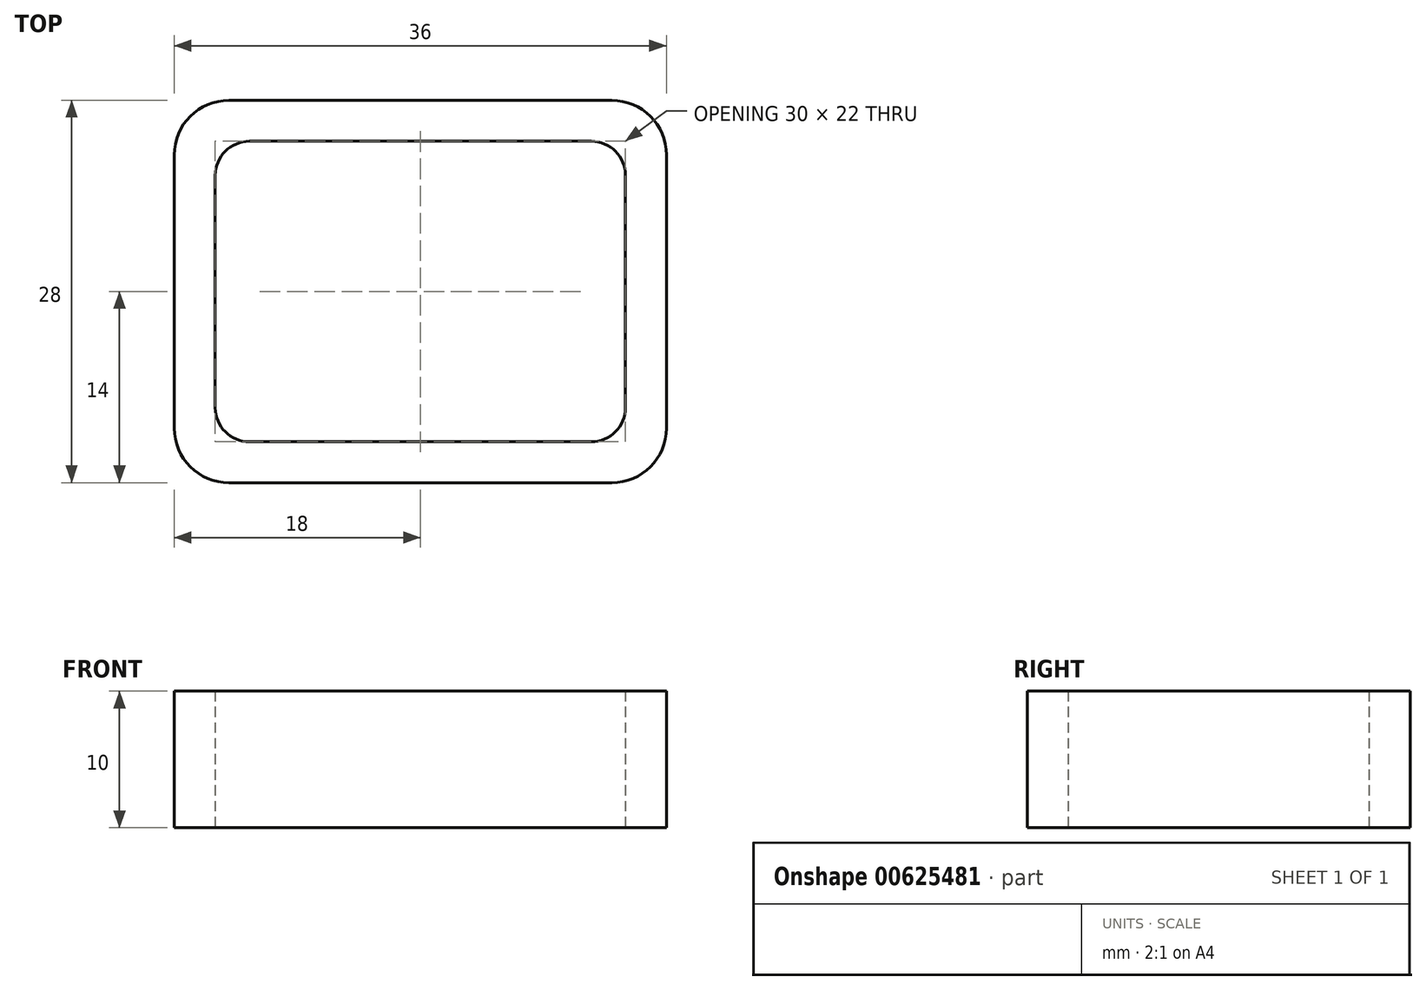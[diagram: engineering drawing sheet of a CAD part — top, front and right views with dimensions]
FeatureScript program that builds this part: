
annotation { "Feature Type Name" : "Feature", "Feature Type Description" : "" }
export const myFeature = defineFeature(function(context is Context, id is Id, definition is map)
    precondition{}
    {
        {
            var Q0;
            Q0=qCreatedBy(makeId("Top.planeOp"),FACE);
            var sketch = newSketch(context, id + "F0", { "sketchPlane" : qUnion([Q0])});
            skLineSegment(sketch, "E0.bottom", {"start": v(18, -14) * mm, "end": v(-18, -14) * mm});
            skLineSegment(sketch, "E0.top", {"start": v(18, 14) * mm, "end": v(-18, 14) * mm});
            skLineSegment(sketch, "E0.left", {"start": v(18, -14) * mm, "end": v(18, 14) * mm});
            skLineSegment(sketch, "E0.right", {"start": v(-18, -14) * mm, "end": v(-18, 14) * mm});
            skPoint(sketch, "E0.middle", {"position": v(0, 0) * mm});
            skSolve(sketch);
        }
        {
            var Q0;
            Q0 = qSketchRegion(id + "F0", true);
            extrude(context, id + "F1", {"entities" : qUnion([Q0]), "depth" : 10 * mm, "offsetDistance" : 25 * mm});
        }
        {
            var Q0;
            Q0=makeQuery(id+"F1.opExtrude","CAP_FACE",FACE,{"disambiguationData":[OSD([sQuery(id+"F0.wireOp",EDGE,"E0.bottom"),sQuery(id+"F0.wireOp",EDGE,"E0.top"),sQuery(id+"F0.wireOp",EDGE,"E0.left"),sQuery(id+"F0.wireOp",EDGE,"E0.right")])],"isStart":false});
            var Q1;
            Q1=makeQuery(id+"F1.opExtrude","CAP_FACE",FACE,{"disambiguationData":[OSD([sQuery(id+"F0.wireOp",EDGE,"E0.bottom"),sQuery(id+"F0.wireOp",EDGE,"E0.top"),sQuery(id+"F0.wireOp",EDGE,"E0.left"),sQuery(id+"F0.wireOp",EDGE,"E0.right")])],"isStart":true});
            shell(context, id + "F2", {"entities" : qUnion([Q0, Q1]), "thickness" : 3 * mm});
        }
        {
            var Q0;
            Q0=makeQuery(id+"F2.opShell","OFFSET_EDGE",EDGE,{"disambiguationData":[OSD([sQuery(id+"F0.wireOp",EDGE,"E0.top"),sQuery(id+"F0.wireOp",EDGE,"E0.right")])]});
            var Q1;
            Q1=makeQuery(id+"F2.opShell","OFFSET_EDGE",EDGE,{"disambiguationData":[OSD([sQuery(id+"F0.wireOp",EDGE,"E0.top"),sQuery(id+"F0.wireOp",EDGE,"E0.left")])]});
            var Q2;
            Q2=makeQuery(id+"F2.opShell","OFFSET_EDGE",EDGE,{"disambiguationData":[OSD([sQuery(id+"F0.wireOp",EDGE,"E0.bottom"),sQuery(id+"F0.wireOp",EDGE,"E0.right")])]});
            var Q3;
            Q3=makeQuery(id+"F2.opShell","OFFSET_EDGE",EDGE,{"disambiguationData":[OSD([sQuery(id+"F0.wireOp",EDGE,"E0.bottom"),sQuery(id+"F0.wireOp",EDGE,"E0.left")])]});
            fillet(context, id + "F3", {"entities" : qUnion([Q0, Q1, Q2, Q3]), "radius" : 2.5 * mm, "tangentPropagation" : true, "allowEdgeOverflow" : false});
        }
        {
            var Q0;
            Q0=makeQuery(id+"F1.opExtrude","SWEPT_EDGE",EDGE,{"disambiguationData":[OSD([sQuery(id+"F0.wireOp",EDGE,"E0.top"),sQuery(id+"F0.wireOp",EDGE,"E0.right")])]});
            var Q1;
            Q1=makeQuery(id+"F1.opExtrude","SWEPT_EDGE",EDGE,{"disambiguationData":[OSD([sQuery(id+"F0.wireOp",EDGE,"E0.top"),sQuery(id+"F0.wireOp",EDGE,"E0.left")])]});
            var Q2;
            Q2=makeQuery(id+"F1.opExtrude","SWEPT_EDGE",EDGE,{"disambiguationData":[OSD([sQuery(id+"F0.wireOp",EDGE,"E0.bottom"),sQuery(id+"F0.wireOp",EDGE,"E0.right")])]});
            var Q3;
            Q3=makeQuery(id+"F1.opExtrude","SWEPT_EDGE",EDGE,{"disambiguationData":[OSD([sQuery(id+"F0.wireOp",EDGE,"E0.bottom"),sQuery(id+"F0.wireOp",EDGE,"E0.left")])]});
            fillet(context, id + "F4", {"entities" : qUnion([Q0, Q1, Q2, Q3]), "radius" : 4 * mm, "tangentPropagation" : true, "allowEdgeOverflow" : false});
        }
    });
